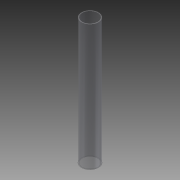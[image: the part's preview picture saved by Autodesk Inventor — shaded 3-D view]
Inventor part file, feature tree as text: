
AUTODESK INVENTOR PART (.ipt)
format: ipt  version: 2015 (Build 190159000, 159)  size: 88,064 bytes
history: native  units: mm
features: extrude x1, sketch x1
ambient origin geometry x8: Origin, YZ Plane, XZ Plane, XY Plane, X Axis, Y Axis, Z Axis, Center Point
bodies: Solid1 (feature_tree)
feature tree (2):
  extrude  "Extrusion1"  [1 undecoded]
  sketch  "Sketch1"  dims[d3=0.0mm]
note: 1 required parameter value undecoded (feature->parameter linkage not recoverable at this tier; creation-order binding heuristic only, values carry confidence <= 0.55)
